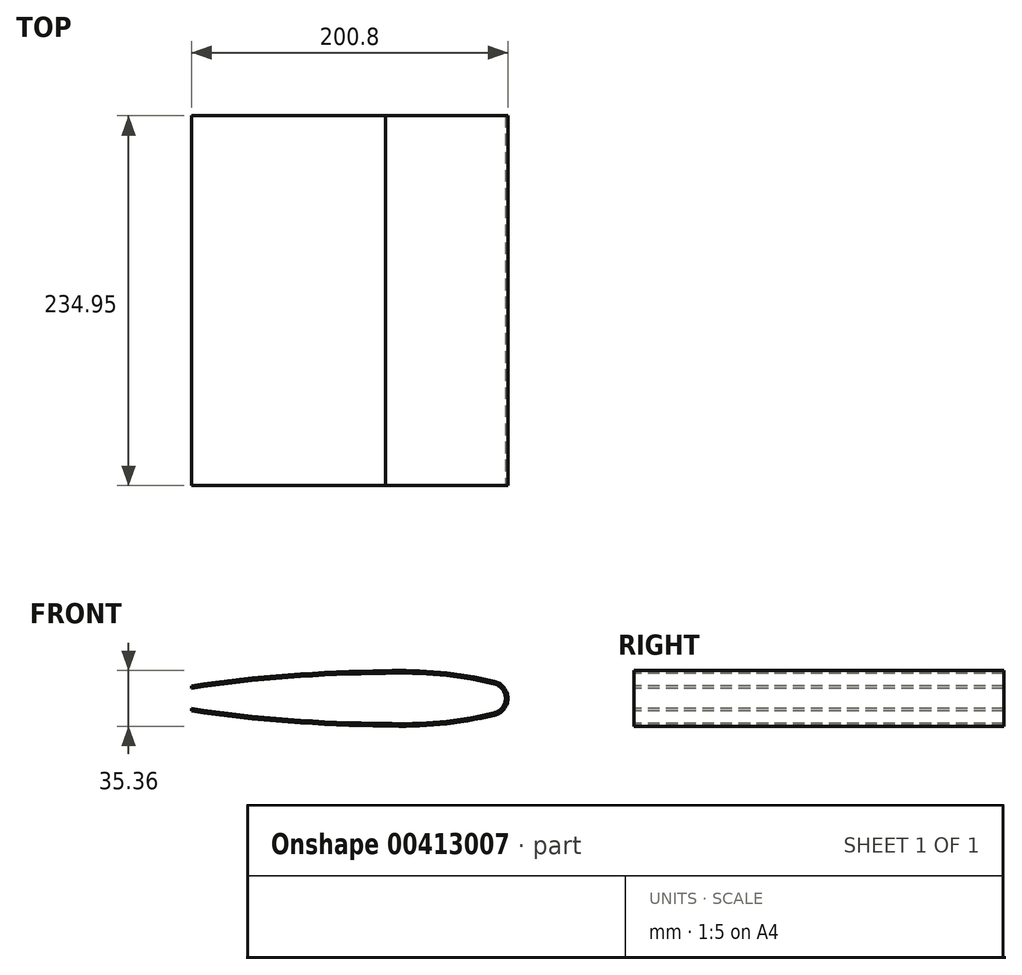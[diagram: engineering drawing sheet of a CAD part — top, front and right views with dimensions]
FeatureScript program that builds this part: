
annotation { "Feature Type Name" : "Feature", "Feature Type Description" : "" }
export const myFeature = defineFeature(function(context is Context, id is Id, definition is map)
    precondition{}
    {
        {
            var Q0;
            Q0=qCreatedBy(makeId("Front.planeOp"),FACE);
            var sketch = newSketch(context, id + "F0", { "sketchPlane" : qUnion([Q0])});
            skLineSegment(sketch, "E0", {"start": v(-126.4, 5.09) * mm, "end": v(-126.4, 6.68) * mm});
            skLineSegment(sketch, "E1", {"start": v(-3.4, 14.47) * mm, "end": v(-3.4, 16.06) * mm});
            skArc(sketch, "E2", {"start": v(-3.4, 16.06) * mm, "mid": v(-65.07, 13.57) * mm, "end": v(-126.4, 6.68) * mm});
            skArc(sketch, "E3", {"start": v(65.84, -12.21) * mm, "mid": v(74.39, -1.4) * mm, "end": v(65.84, 9.4) * mm});
            skLineSegment(sketch, "E4", {"start": v(-126.4, -7.9) * mm, "end": v(-126.4, -9.48) * mm});
            skLineSegment(sketch, "E5", {"start": v(-3.4, -17.28) * mm, "end": v(-3.4, -18.86) * mm});
            skArc(sketch, "E6", {"start": v(-126.4, -9.48) * mm, "mid": v(-65.07, -16.37) * mm, "end": v(-3.4, -18.86) * mm});
            skArc(sketch, "E7", {"start": v(-3.4, -18.86) * mm, "mid": v(31.45, -17.92) * mm, "end": v(65.84, -12.21) * mm});
            skArc(sketch, "E8.trimOffspring", {"start": v(65.84, 9.4) * mm, "mid": v(31.45, 15.12) * mm, "end": v(-3.4, 16.06) * mm});
            skArc(sketch, "E9", {"start": v(-3.4, 14.47) * mm, "mid": v(-65.07, 11.98) * mm, "end": v(-126.4, 5.09) * mm});
            skArc(sketch, "E10", {"start": v(-126.4, -7.9) * mm, "mid": v(-65.07, -14.78) * mm, "end": v(-3.4, -17.28) * mm});
            skArc(sketch, "E11", {"start": v(-3.4, -17.28) * mm, "mid": v(31.26, -16.33) * mm, "end": v(65.47, -10.67) * mm});
            skArc(sketch, "E12", {"start": v(65.47, 7.87) * mm, "mid": v(31.26, 13.53) * mm, "end": v(-3.4, 14.47) * mm});
            skCircle(sketch, "E13", {"center": v(63.28, -1.4) * mm, "radius": 9.53 * mm});
            skSolve(sketch);
        }
        {
            var Q0;
            Q0=makeQuery(id+"F0.imprint","IMPRINT",FACE,{"disambiguationData":[TD([[makeQuery(id+"F0.imprint","IMPRINT",EDGE,{"derivedFrom":sQuery(id+"F0.wireOp",EDGE,"E0")}),-1.0]])]});
            var Q1;
            Q1=makeQuery(id+"F0.imprint","IMPRINT",FACE,{"disambiguationData":[TD([[makeQuery(id+"F0.imprint","IMPRINT",EDGE,{"derivedFrom":sQuery(id+"F0.wireOp",EDGE,"E4")}),1.0]])]});
            var Q2;
            Q2=makeQuery(id+"F0.imprint","IMPRINT",FACE,{"disambiguationData":[TD([[makeQuery(id+"F0.imprint","IMPRINT",EDGE,{"derivedFrom":sQuery(id+"F0.wireOp",EDGE,"E1")}),-1.0]])]});
            extrude(context, id + "F1", {"entities" : qUnion([Q0, Q1, Q2]), "oppositeDirection" : true, "depth" : 234.95 * mm});
        }
    });
